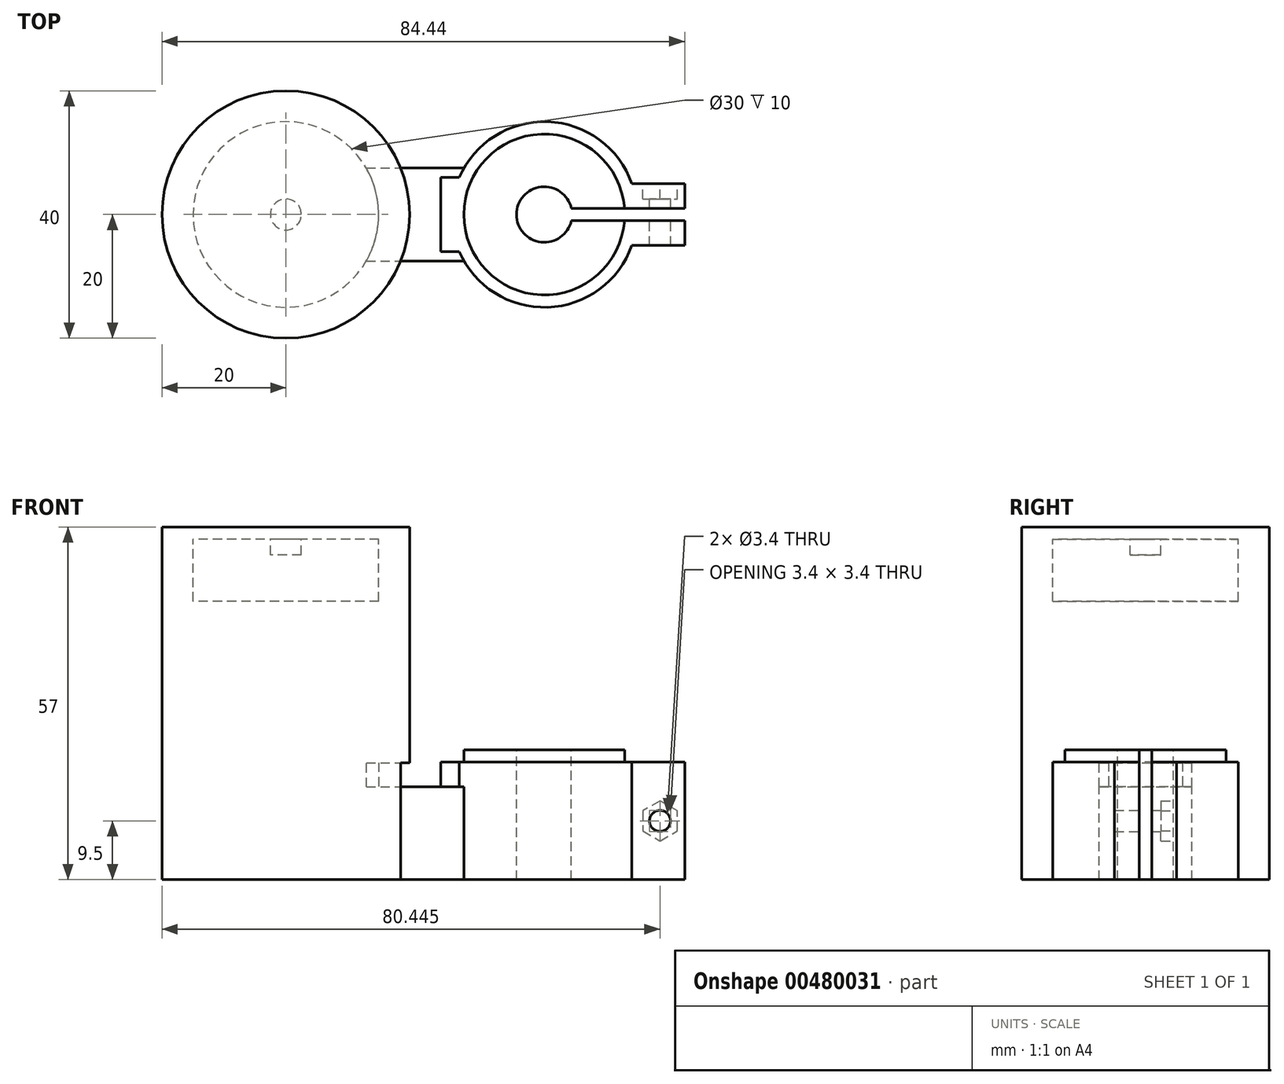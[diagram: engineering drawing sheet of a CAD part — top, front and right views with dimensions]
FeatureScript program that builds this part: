
annotation { "Feature Type Name" : "Feature", "Feature Type Description" : "" }
export const myFeature = defineFeature(function(context is Context, id is Id, definition is map)
    precondition{}
    {
        {
            var Q0;
            Q0=qCreatedBy(makeId("Top.planeOp"),FACE);
            var sketch = newSketch(context, id + "F0", { "sketchPlane" : qUnion([Q0])});
            skArc(sketch, "E0", {"start": v(52.7, 1) * mm, "mid": v(30.75, 0) * mm, "end": v(52.7, -1) * mm});
            skArc(sketch, "E1", {"start": v(56.44, 3) * mm, "mid": v(26.75, 0) * mm, "end": v(56.44, -3) * mm});
            skLineSegment(sketch, "E2.bottom", {"start": v(56.44, 3) * mm, "end": v(64.44, 3) * mm});
            skLineSegment(sketch, "E2.top", {"start": v(56.44, -3) * mm, "end": v(64.44, -3) * mm});
            skLineSegment(sketch, "E2.left", {"start": v(56.44, 3) * mm, "end": v(56.44, 1) * mm, "construction": true});
            skLineSegment(sketch, "E2.right", {"start": v(64.44, 3) * mm, "end": v(64.44, 1) * mm});
            skLineSegment(sketch, "E3", {"start": v(64.44, -1) * mm, "end": v(56.44, -1) * mm});
            skLineSegment(sketch, "E4", {"start": v(64.44, 1) * mm, "end": v(56.44, 1) * mm});
            skLineSegment(sketch, "E5", {"start": v(64.44, 1) * mm, "end": v(64.44, -1) * mm, "construction": true});
            skLineSegment(sketch, "E6", {"start": v(64.44, -1) * mm, "end": v(64.44, -3) * mm});
            skLineSegment(sketch, "E7", {"start": v(56.44, -1) * mm, "end": v(56.44, -3) * mm, "construction": true});
            skLineSegment(sketch, "E8", {"start": v(56.44, 1) * mm, "end": v(56.44, -1) * mm, "construction": true});
            skLineSegment(sketch, "E9", {"start": v(56.44, 1) * mm, "end": v(52.7, 1) * mm});
            skLineSegment(sketch, "E10", {"start": v(56.44, -1) * mm, "end": v(52.7, -1) * mm});
            skCircle(sketch, "E11.0", {"center": v(0, 0) * mm, "radius": 15 * mm});
            skLineSegment(sketch, "E12", {"start": v(13, 7.5) * mm, "end": v(28.76, 7.5) * mm});
            skLineSegment(sketch, "E13", {"start": v(13, -7.5) * mm, "end": v(28.76, -7.5) * mm});
            skLineSegment(sketch, "E14", {"start": v(0, 0) * mm, "end": v(15, 0) * mm, "construction": true});
            skLineSegment(sketch, "E15", {"start": v(26.75, 0) * mm, "end": v(41.75, 0) * mm, "construction": true});
            skLineSegment(sketch, "E16", {"start": v(15, 0) * mm, "end": v(26.75, 0) * mm, "construction": true});
            skLineSegment(sketch, "E17", {"start": v(28, 6) * mm, "end": v(25, 6) * mm});
            skLineSegment(sketch, "E18", {"start": v(25, 6) * mm, "end": v(25, 0) * mm});
            skLineSegment(sketch, "E19", {"start": v(25, 0) * mm, "end": v(25, -6) * mm});
            skLineSegment(sketch, "E20", {"start": v(25, -6) * mm, "end": v(28, -6) * mm});
            skSolve(sketch);
        }
        {
            var Q0;
            {var subQ0=sQuery(id+"F0.wireOp",EDGE,"E17");Q0=makeQuery(id+"F0.imprint","IMPRINT",FACE,{"disambiguationData":[TD([[makeQuery(id+"F0.imprint","IMPRINT",EDGE,{"derivedFrom":subQ0}),1.0]])]});}
            var Q1;
            Q1=makeQuery(id+"F0.imprint","IMPRINT",FACE,{"disambiguationData":[TD([[makeQuery(id+"F0.imprint","IMPRINT",EDGE,{"derivedFrom":sQuery(id+"F0.wireOp",EDGE,"E0")}),-1.0]])]});
            extrude(context, id + "F1", {"entities" : qUnion([Q0, Q1]), "depth" : 4 * mm});
        }
        {
            var Q0;
            Q0=makeQuery(id+"F0.imprint","IMPRINT",FACE,{"disambiguationData":[TD([[makeQuery(id+"F0.imprint","IMPRINT",EDGE,{"derivedFrom":sQuery(id+"F0.wireOp",EDGE,"E0")}),-1.0]])]});
            var Q1;
            {var subQ0=sQuery(id+"F0.wireOp",EDGE,"E17");Q1=makeQuery(id+"F0.imprint","IMPRINT",FACE,{"disambiguationData":[TD([[makeQuery(id+"F0.imprint","IMPRINT",EDGE,{"derivedFrom":subQ0}),1.0]])]});}
            var Q2;
            {var subQ0=sQuery(id+"F0.wireOp",EDGE,"E12");Q2=makeQuery(id+"F0.imprint","IMPRINT",FACE,{"disambiguationData":[TD([[makeQuery(id+"F0.imprint","IMPRINT",EDGE,{"derivedFrom":subQ0}),-1.0]])]});}
            extrude(context, id + "F2", {"entities" : qUnion([Q0, Q1, Q2]), "operationType" : NewBodyOperationType.ADD, "oppositeDirection" : true, "depth" : 15 * mm});
        }
        {
            var Q0;
            {var subQ0=sQuery(id+"F0.wireOp",EDGE,"E11.0");var subQ1=makeQuery(id+"F0.imprint","INTERSECT",VERTEX,{"derivedFrom":[subQ0,sQuery(id+"F0.wireOp",EDGE,"E12")]});Q0=makeQuery(id+"F0.imprint","IMPRINT",FACE,{"disambiguationData":[TD([[makeQuery(id+"F0.imprint","IMPRINT",EDGE,{"disambiguationData":[TD([[subQ1,-1.0]])],"derivedFrom":subQ0}),1.0]])]});}
            var Q1;
            Q1=makeQuery(id+"F2.opExtrude","CAP_FACE",FACE,{"disambiguationData":[OSD([sQuery(id+"F0.wireOp",EDGE,"E0"),sQuery(id+"F0.wireOp",EDGE,"E1"),sQuery(id+"F0.wireOp",EDGE,"E2.bottom"),sQuery(id+"F0.wireOp",EDGE,"E2.top"),sQuery(id+"F0.wireOp",EDGE,"E2.right"),sQuery(id+"F0.wireOp",EDGE,"E3"),sQuery(id+"F0.wireOp",EDGE,"E4"),sQuery(id+"F0.wireOp",EDGE,"E6"),sQuery(id+"F0.wireOp",EDGE,"E9"),sQuery(id+"F0.wireOp",EDGE,"E10"),sQuery(id+"F0.wireOp",EDGE,"E11.0"),sQuery(id+"F0.wireOp",EDGE,"E12"),sQuery(id+"F0.wireOp",EDGE,"E13")])],"isStart":false});
            extrude(context, id + "F3", {"entities" : qUnion([Q0]), "operationType" : NewBodyOperationType.ADD, "depth" : 30 * mm, "hasSecondDirection" : true, "secondDirectionBound" : SecondDirectionBoundingType.UP_TO_SURFACE, "secondDirectionOppositeDirection" : true, "secondDirectionBoundEntityFace" : qUnion([Q1]), "secondDirectionDepth" : 5.4 * mm});
        }
        {
            var Q0;
            Q0=makeQuery(id+"F2.opExtrude","SWEPT_FACE",FACE,{"disambiguationData":[OSD([sQuery(id+"F0.wireOp",EDGE,"E2.bottom")])]});
            var sketch = newSketch(context, id + "F4", { "sketchPlane" : qUnion([Q0])});
            skLineSegment(sketch, "E21", {"start": v(-60.44, -15) * mm, "end": v(-60.44, 4) * mm, "construction": true});
            skCircle(sketch, "E22.cCircle", {"center": v(-60.44, -5.5) * mm, "radius": 2.8 * mm, "construction": true});
            skLineSegment(sketch, "E22.0", {"start": v(-60.44, -8.73) * mm, "end": v(-63.24, -7.12) * mm});
            skLineSegment(sketch, "E22.1", {"start": v(-63.24, -7.12) * mm, "end": v(-63.24, -3.88) * mm});
            skLineSegment(sketch, "E22.2", {"start": v(-63.24, -3.88) * mm, "end": v(-60.44, -2.27) * mm});
            skLineSegment(sketch, "E22.3", {"start": v(-60.44, -2.27) * mm, "end": v(-57.64, -3.88) * mm});
            skLineSegment(sketch, "E22.4", {"start": v(-57.64, -3.88) * mm, "end": v(-57.64, -7.12) * mm});
            skLineSegment(sketch, "E22.5", {"start": v(-57.64, -7.12) * mm, "end": v(-60.44, -8.73) * mm});
            skPoint(sketch, "E22.0.midPoint", {"position": v(-61.84, -7.92) * mm});
            skCircle(sketch, "E23", {"center": v(-60.44, -5.5) * mm, "radius": 1.7 * mm});
            skSolve(sketch);
        }
        {
            var Q0;
            Q0=makeQuery(id+"F4.imprint","IMPRINT",FACE,{"disambiguationData":[TD([[makeQuery(id+"F4.imprint","IMPRINT",EDGE,{"derivedFrom":sQuery(id+"F4.wireOp",EDGE,"E22.0")}),-1.0]])]});
            var Q1;
            Q1=sQuery(id+"F4.wireOp",EDGE,"E21");
            var Q2;
            Q2=sQuery(id+"F4.wireOp",EDGE,"E22.1");
            var Q3;
            Q3=sQuery(id+"F4.wireOp",EDGE,"E22.0");
            extrude(context, id + "F5", {"entities" : qUnion([Q0]), "operationType" : NewBodyOperationType.REMOVE, "surfaceEntities" : qUnion([Q1, Q2, Q3]), "oppositeDirection" : true, "depth" : 0.5 * mm});
        }
        {
            var Q0;
            Q0=makeQuery(id+"F5.boolean.opBoolean","SPLIT",FACE,{"disambiguationData":[TD([makeQuery(id+"F5.opExtrude","SWEPT_FACE",FACE,{"disambiguationData":[OSD([sQuery(id+"F4.wireOp",EDGE,"E23")])]})])],"derivedFrom":makeQuery(id+"F2.opExtrude","SWEPT_FACE",FACE,{"disambiguationData":[OSD([sQuery(id+"F0.wireOp",EDGE,"E2.bottom")])]})});
            var Q1;
            Q1=makeQuery(id+"F2.opExtrude","SWEPT_FACE",FACE,{"disambiguationData":[OSD([sQuery(id+"F0.wireOp",EDGE,"E2.top")])]});
            extrude(context, id + "F6", {"entities" : qUnion([Q0]), "operationType" : NewBodyOperationType.REMOVE, "endBound" : BoundingType.UP_TO_SURFACE, "oppositeDirection" : true, "endBoundEntityFace" : qUnion([Q1]), "depth" : 2.53 * mm});
        }
        {
            var Q0;
            Q0=makeQuery(id+"F1.opExtrude","CAP_FACE",FACE,{"disambiguationData":[OSD([sQuery(id+"F0.wireOp",EDGE,"E0"),sQuery(id+"F0.wireOp",EDGE,"E1"),sQuery(id+"F0.wireOp",EDGE,"E2.bottom"),sQuery(id+"F0.wireOp",EDGE,"E2.top"),sQuery(id+"F0.wireOp",EDGE,"E2.right"),sQuery(id+"F0.wireOp",EDGE,"E3"),sQuery(id+"F0.wireOp",EDGE,"E4"),sQuery(id+"F0.wireOp",EDGE,"E6"),sQuery(id+"F0.wireOp",EDGE,"E9"),sQuery(id+"F0.wireOp",EDGE,"E10"),sQuery(id+"F0.wireOp",EDGE,"E17"),sQuery(id+"F0.wireOp",EDGE,"E18"),sQuery(id+"F0.wireOp",EDGE,"E19"),sQuery(id+"F0.wireOp",EDGE,"E20")])],"isStart":false});
            var sketch = newSketch(context, id + "F7", { "sketchPlane" : qUnion([Q0])});
            skArc(sketch, "E24.0", {"start": v(52.7, 1) * mm, "mid": v(30.75, 0) * mm, "end": v(52.7, -1) * mm});
            skArc(sketch, "E25.0", {"start": v(46.14, 1) * mm, "mid": v(37.25, 0) * mm, "end": v(46.14, -1) * mm});
            skLineSegment(sketch, "E26", {"start": v(46.14, -1) * mm, "end": v(52.7, -1) * mm});
            skLineSegment(sketch, "E27", {"start": v(46.14, 1) * mm, "end": v(52.7, 1) * mm});
            skArc(sketch, "E28.0", {"start": v(54.7, 1) * mm, "mid": v(28.75, 0) * mm, "end": v(54.7, -1) * mm});
            skLineSegment(sketch, "E29", {"start": v(52.7, -1) * mm, "end": v(54.7, -1) * mm});
            skLineSegment(sketch, "E30", {"start": v(52.7, 1) * mm, "end": v(54.7, 1) * mm});
            skSolve(sketch);
        }
        {
            var Q0;
            Q0=makeQuery(id+"F7.imprint","IMPRINT",FACE,{"disambiguationData":[TD([[makeQuery(id+"F7.imprint","IMPRINT",EDGE,{"derivedFrom":sQuery(id+"F7.wireOp",EDGE,"E24.0")}),1.0]])]});
            var Q1;
            {var subQ0=sQuery(id+"F0.wireOp",EDGE,"E11.0");Q1=makeQuery(id+"F3.boolean.opBoolean","MERGE",FACE,{"derivedFrom":[makeQuery(id+"F2.opExtrude","CAP_FACE",FACE,{"disambiguationData":[OSD([sQuery(id+"F0.wireOp",EDGE,"E0"),sQuery(id+"F0.wireOp",EDGE,"E1"),sQuery(id+"F0.wireOp",EDGE,"E2.bottom"),sQuery(id+"F0.wireOp",EDGE,"E2.top"),sQuery(id+"F0.wireOp",EDGE,"E2.right"),sQuery(id+"F0.wireOp",EDGE,"E3"),sQuery(id+"F0.wireOp",EDGE,"E4"),sQuery(id+"F0.wireOp",EDGE,"E6"),sQuery(id+"F0.wireOp",EDGE,"E9"),sQuery(id+"F0.wireOp",EDGE,"E10"),subQ0,sQuery(id+"F0.wireOp",EDGE,"E12"),sQuery(id+"F0.wireOp",EDGE,"E13")])],"isStart":false}),makeQuery(id+"F3.opExtrude","CAP_FACE",FACE,{"disambiguationData":[OSD([subQ0])],"isStart":true})]});}
            extrude(context, id + "F8", {"entities" : qUnion([Q0]), "endBound" : BoundingType.UP_TO_SURFACE, "oppositeDirection" : true, "endBoundEntityFace" : qUnion([Q1]), "depth" : 20 * mm});
        }
        {
            var Q0;
            Q0=qSketchRegion(id+"F7",true);
            extrude(context, id + "F9", {"entities" : qUnion([Q0]), "operationType" : NewBodyOperationType.ADD, "depth" : 2 * mm});
        }
        {
            var Q0;
            {var subQ4=sQuery(id+"F0.wireOp",EDGE,"E2.bottom");var subQ6=sQuery(id+"F0.wireOp",EDGE,"E2.right");Q0=makeQuery(id+"F5.boolean.opBoolean","SPLIT",FACE,{"disambiguationData":[TD([makeQuery(id+"F1.opExtrude","SWEPT_FACE",FACE,{"disambiguationData":[OSD([subQ6])]})])],"derivedFrom":makeQuery(id+"F2.boolean.opBoolean","MERGE",FACE,{"derivedFrom":[makeQuery(id+"F1.opExtrude","SWEPT_FACE",FACE,{"disambiguationData":[OSD([subQ4])]}),makeQuery(id+"F2.opExtrude","SWEPT_FACE",FACE,{"disambiguationData":[OSD([subQ4])]})]})});}
            var sketch = newSketch(context, id + "F10", { "sketchPlane" : qUnion([Q0])});
            skLineSegment(sketch, "E31.0", {"start": v(-63.24, -3.88) * mm, "end": v(-60.44, -2.27) * mm});
            skLineSegment(sketch, "E31.1", {"start": v(-60.44, -2.27) * mm, "end": v(-57.64, -3.88) * mm});
            skLineSegment(sketch, "E31.2", {"start": v(-57.64, -3.88) * mm, "end": v(-57.64, -7.12) * mm});
            skLineSegment(sketch, "E31.3", {"start": v(-57.64, -7.12) * mm, "end": v(-60.44, -8.73) * mm});
            skLineSegment(sketch, "E31.4", {"start": v(-60.44, -8.73) * mm, "end": v(-63.24, -7.12) * mm});
            skLineSegment(sketch, "E31.5", {"start": v(-63.24, -7.12) * mm, "end": v(-63.24, -3.88) * mm});
            skLineSegment(sketch, "E31.6", {"start": v(-56.44, -15) * mm, "end": v(-64.44, -15) * mm});
            skLineSegment(sketch, "E31.7", {"start": v(-64.44, 4) * mm, "end": v(-64.44, -15) * mm});
            skLineSegment(sketch, "E31.8", {"start": v(-56.44, 4) * mm, "end": v(-64.44, 4) * mm});
            skLineSegment(sketch, "E32", {"start": v(-56.44, 4) * mm, "end": v(-52.5, 4) * mm});
            skLineSegment(sketch, "E33", {"start": v(-52.5, 4) * mm, "end": v(-52.5, -15) * mm});
            skLineSegment(sketch, "E34", {"start": v(-52.5, -15) * mm, "end": v(-56.44, -15) * mm});
            skSolve(sketch);
        }
        {
            var Q0;
            Q0=qSketchRegion(id+"F10",true);
            extrude(context, id + "F11", {"entities" : qUnion([Q0]), "operationType" : NewBodyOperationType.ADD, "depth" : 2 * mm});
        }
        {
            var Q0;
            {var subQ0=sQuery(id+"F0.wireOp",EDGE,"E2.top");Q0=makeQuery(id+"F2.boolean.opBoolean","MERGE",FACE,{"derivedFrom":[makeQuery(id+"F1.opExtrude","SWEPT_FACE",FACE,{"disambiguationData":[OSD([subQ0])]}),makeQuery(id+"F2.opExtrude","SWEPT_FACE",FACE,{"disambiguationData":[OSD([subQ0])]})]});}
            var sketch = newSketch(context, id + "F12", { "sketchPlane" : qUnion([Q0])});
            skCircle(sketch, "E35.0", {"center": v(60.44, -5.5) * mm, "radius": 1.7 * mm});
            skLineSegment(sketch, "E35.1", {"start": v(56.44, 4) * mm, "end": v(64.44, 4) * mm});
            skLineSegment(sketch, "E35.2", {"start": v(64.44, 4) * mm, "end": v(64.44, -15) * mm});
            skLineSegment(sketch, "E35.3", {"start": v(56.44, -15) * mm, "end": v(64.44, -15) * mm});
            skLineSegment(sketch, "E36", {"start": v(56.44, -15) * mm, "end": v(52.15, -15) * mm});
            skLineSegment(sketch, "E37", {"start": v(52.15, -15) * mm, "end": v(52.15, 4) * mm});
            skLineSegment(sketch, "E38", {"start": v(52.15, 4) * mm, "end": v(56.44, 4) * mm});
            skSolve(sketch);
        }
        {
            var Q0;
            Q0=qSketchRegion(id+"F12",true);
            extrude(context, id + "F13", {"entities" : qUnion([Q0]), "operationType" : NewBodyOperationType.ADD, "depth" : 2 * mm});
        }
        {
            var Q0;
            Q0=makeQuery(id+"F3.opExtrude","CAP_FACE",FACE,{"disambiguationData":[OSD([sQuery(id+"F0.wireOp",EDGE,"E11.0")])],"isStart":false});
            cPlane(context, id + "F14", {"entities" : qUnion([Q0]), "cplaneType" : CPlaneType.OFFSET, "offset" : 10 * mm, "width" : 150 * mm, "height" : 150 * mm});
        }
        {
            var Q0;
            Q0=qCreatedBy(id+"F14.planeOp",FACE);
            var sketch = newSketch(context, id + "F15", { "sketchPlane" : qUnion([Q0])});
            skCircle(sketch, "E39.0", {"center": v(0, 0) * mm, "radius": 15 * mm});
            skCircle(sketch, "E40", {"center": v(0, 0) * mm, "radius": 2.5 * mm});
            skCircle(sketch, "E41.0", {"center": v(0, 0) * mm, "radius": 20 * mm});
            skSolve(sketch);
        }
        {
            var Q0;
            Q0=makeQuery(id+"F15.imprint","IMPRINT",FACE,{"disambiguationData":[TD([[makeQuery(id+"F15.imprint","IMPRINT",EDGE,{"derivedFrom":sQuery(id+"F15.wireOp",EDGE,"E40")}),1.0]])]});
            extrude(context, id + "F16", {"entities" : qUnion([Q0]), "oppositeDirection" : true, "depth" : 2.5 * mm});
        }
        {
            var Q0;
            Q0=makeQuery(id+"F15.imprint","IMPRINT",FACE,{"disambiguationData":[TD([[makeQuery(id+"F15.imprint","IMPRINT",EDGE,{"derivedFrom":sQuery(id+"F15.wireOp",EDGE,"E39.0")}),-1.0]])]});
            extrude(context, id + "F17", {"entities" : qUnion([Q0]), "operationType" : NewBodyOperationType.ADD, "oppositeDirection" : true, "depth" : 36.1 * mm});
        }
        {
            var Q0;
            Q0=makeQuery(id+"F15.imprint","IMPRINT",FACE,{"disambiguationData":[TD([[makeQuery(id+"F15.imprint","IMPRINT",EDGE,{"derivedFrom":sQuery(id+"F15.wireOp",EDGE,"E39.0")}),-1.0]])]});
            var Q1;
            Q1=makeQuery(id+"F15.imprint","IMPRINT",FACE,{"disambiguationData":[TD([[makeQuery(id+"F15.imprint","IMPRINT",EDGE,{"derivedFrom":sQuery(id+"F15.wireOp",EDGE,"E39.0")}),1.0]])]});
            var Q2;
            Q2=makeQuery(id+"F15.imprint","IMPRINT",FACE,{"disambiguationData":[TD([[makeQuery(id+"F15.imprint","IMPRINT",EDGE,{"derivedFrom":sQuery(id+"F15.wireOp",EDGE,"E40")}),1.0]])]});
            extrude(context, id + "F18", {"entities" : qUnion([Q0, Q1, Q2]), "operationType" : NewBodyOperationType.ADD, "depth" : 2 * mm});
        }
        {
            var Q0;
            Q0=makeQuery(id+"F17.opExtrude","CAP_FACE",FACE,{"disambiguationData":[OSD([sQuery(id+"F15.wireOp",EDGE,"E39.0"),sQuery(id+"F15.wireOp",EDGE,"E41.0")])],"isStart":false});
            var sketch = newSketch(context, id + "F19", { "sketchPlane" : qUnion([Q0])});
            skLineSegment(sketch, "E42.0.10", {"start": v(52.7, -1) * mm, "end": v(52.7, -1) * mm});
            skLineSegment(sketch, "E43.0", {"start": v(13, 7.5) * mm, "end": v(28.76, 7.5) * mm});
            skLineSegment(sketch, "E44.0", {"start": v(13, -7.5) * mm, "end": v(28.76, -7.5) * mm});
            skCircle(sketch, "E45.0", {"center": v(0, 0) * mm, "radius": 15 * mm});
            skSolve(sketch);
        }
        {
            var Q0;
            {var subQ0=sQuery(id+"F19.wireOp",EDGE,"E45.0");var subQ1=sQuery(id+"F19.wireOp",EDGE,"E43.0");var subQ2=makeQuery(id+"F19.imprint","INTERSECT",VERTEX,{"derivedFrom":[subQ1,subQ0]});Q0=makeQuery(id+"F19.imprint","IMPRINT",FACE,{"disambiguationData":[TD([[makeQuery(id+"F19.imprint","IMPRINT",EDGE,{"disambiguationData":[TD([[subQ2,-1.0]])],"derivedFrom":subQ1}),1.0]])]});}
            var Q1;
            {var subQ0=sQuery(id+"F0.wireOp",EDGE,"E11.0");Q1=makeQuery(id+"F13.boolean.opBoolean","MERGE",FACE,{"derivedFrom":[makeQuery(id+"F11.boolean.opBoolean","MERGE",FACE,{"derivedFrom":[makeQuery(id+"F3.boolean.opBoolean","MERGE",FACE,{"derivedFrom":[makeQuery(id+"F2.opExtrude","CAP_FACE",FACE,{"disambiguationData":[OSD([sQuery(id+"F0.wireOp",EDGE,"E0"),sQuery(id+"F0.wireOp",EDGE,"E1"),sQuery(id+"F0.wireOp",EDGE,"E2.bottom"),sQuery(id+"F0.wireOp",EDGE,"E2.top"),sQuery(id+"F0.wireOp",EDGE,"E2.right"),sQuery(id+"F0.wireOp",EDGE,"E3"),sQuery(id+"F0.wireOp",EDGE,"E4"),sQuery(id+"F0.wireOp",EDGE,"E6"),sQuery(id+"F0.wireOp",EDGE,"E9"),sQuery(id+"F0.wireOp",EDGE,"E10"),subQ0,sQuery(id+"F0.wireOp",EDGE,"E12"),sQuery(id+"F0.wireOp",EDGE,"E13")])],"isStart":false}),makeQuery(id+"F3.opExtrude","CAP_FACE",FACE,{"disambiguationData":[OSD([subQ0])],"isStart":true})]}),makeQuery(id+"F11.opExtrude","SWEPT_FACE",FACE,{"disambiguationData":[OSD([sQuery(id+"F10.wireOp",EDGE,"E31.6"),sQuery(id+"F10.wireOp",EDGE,"E34")])]})]}),makeQuery(id+"F13.opExtrude","SWEPT_FACE",FACE,{"disambiguationData":[OSD([sQuery(id+"F12.wireOp",EDGE,"E35.3"),sQuery(id+"F12.wireOp",EDGE,"E36")])]})]});}
            extrude(context, id + "F20", {"entities" : qUnion([Q0]), "operationType" : NewBodyOperationType.ADD, "endBound" : BoundingType.UP_TO_SURFACE, "endBoundEntityFace" : qUnion([Q1]), "depth" : 25 * mm});
        }
    });
